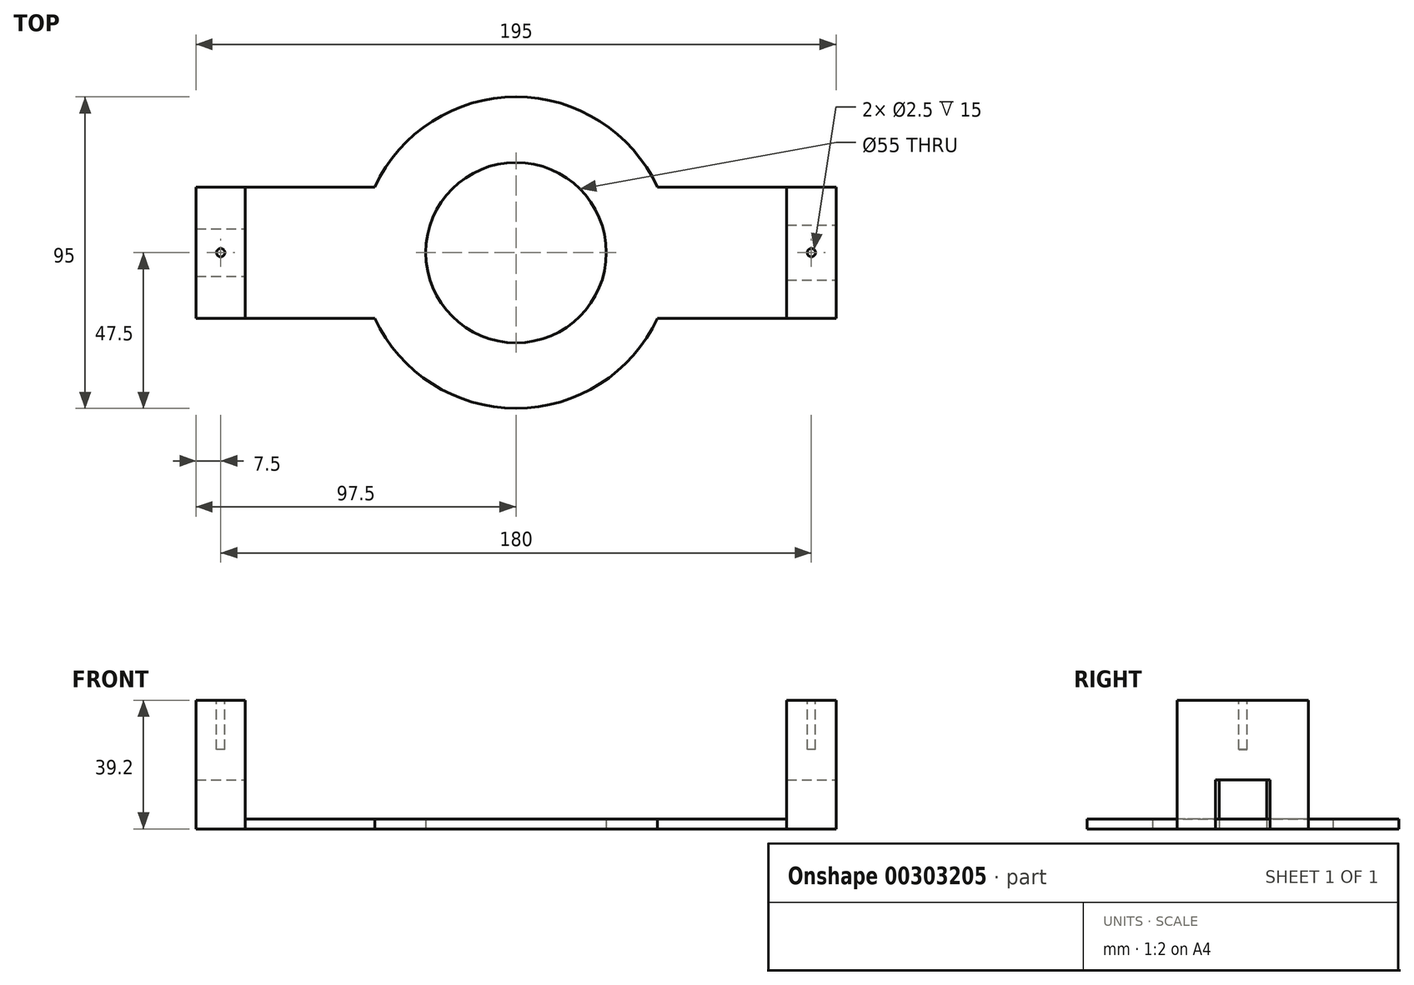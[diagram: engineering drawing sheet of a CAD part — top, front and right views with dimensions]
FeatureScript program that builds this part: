
annotation { "Feature Type Name" : "Feature", "Feature Type Description" : "" }
export const myFeature = defineFeature(function(context is Context, id is Id, definition is map)
    precondition{}
    {
        {
            var Q0;
            Q0=qCreatedBy(makeId("Top.planeOp"),FACE);
            var sketch = newSketch(context, id + "F0", { "sketchPlane" : qUnion([Q0])});
            skCircle(sketch, "E0", {"center": v(0, 0) * mm, "radius": 27.5 * mm});
            skCircle(sketch, "E1", {"center": v(0, 0) * mm, "radius": 47.5 * mm});
            skLineSegment(sketch, "E2", {"start": v(0, 0) * mm, "end": v(-90, 0) * mm});
            skLineSegment(sketch, "E3", {"start": v(0, 0) * mm, "end": v(90, 0) * mm});
            skLineSegment(sketch, "E4.bottom", {"start": v(-97.5, 20) * mm, "end": v(-82.5, 20) * mm});
            skLineSegment(sketch, "E4.top", {"start": v(-97.5, -20) * mm, "end": v(-82.5, -20) * mm});
            skLineSegment(sketch, "E4.left", {"start": v(-97.5, 20) * mm, "end": v(-97.5, -20) * mm});
            skLineSegment(sketch, "E4.right", {"start": v(-82.5, 20) * mm, "end": v(-82.5, -20) * mm});
            skPoint(sketch, "E4.middle", {"position": v(-90, 0) * mm});
            skLineSegment(sketch, "E5.bottom", {"start": v(82.5, 20) * mm, "end": v(97.5, 20) * mm});
            skLineSegment(sketch, "E5.top", {"start": v(82.5, -20) * mm, "end": v(97.5, -20) * mm});
            skLineSegment(sketch, "E5.left", {"start": v(82.5, 20) * mm, "end": v(82.5, -20) * mm});
            skLineSegment(sketch, "E5.right", {"start": v(97.5, 20) * mm, "end": v(97.5, -20) * mm});
            skPoint(sketch, "E5.middle", {"position": v(90, 0) * mm});
            skLineSegment(sketch, "E6.left", {"start": v(-82.5, 20) * mm, "end": v(-82.5, -20.66) * mm});
            skLineSegment(sketch, "E7.left", {"start": v(82.5, 20) * mm, "end": v(82.5, -20.66) * mm});
            skLineSegment(sketch, "E8", {"start": v(97.5, -20) * mm, "end": v(43.08, -20) * mm});
            skLineSegment(sketch, "E9", {"start": v(97.5, 20) * mm, "end": v(43.08, 20) * mm});
            skLineSegment(sketch, "E10", {"start": v(-97.5, -20) * mm, "end": v(-43.08, -20) * mm});
            skLineSegment(sketch, "E11", {"start": v(-97.5, 20) * mm, "end": v(-43.08, 20) * mm});
            skSolve(sketch);
        }
        {
            var Q0;
            {var subQ3=sQuery(id+"F0.wireOp",EDGE,"E4.bottom");Q0=makeQuery(id+"F0.imprint","IMPRINT",FACE,{"disambiguationData":[TD([[makeQuery(id+"F0.imprint","IMPRINT",EDGE,{"derivedFrom":subQ3}),-1.0]])]});}
            var Q1;
            {var subQ3=sQuery(id+"F0.wireOp",EDGE,"E5.bottom");Q1=makeQuery(id+"F0.imprint","IMPRINT",FACE,{"disambiguationData":[TD([[makeQuery(id+"F0.imprint","IMPRINT",EDGE,{"derivedFrom":subQ3}),-1.0]])]});}
            extrude(context, id + "F1", {"entities" : qUnion([Q0, Q1]), "depth" : 39.2 * mm, "offsetDistance" : 25 * mm});
        }
        {
            var Q0;
            {var subQ3=sQuery(id+"F0.wireOp",EDGE,"E9");Q0=makeQuery(id+"F0.imprint","IMPRINT",FACE,{"disambiguationData":[TD([[makeQuery(id+"F0.imprint","IMPRINT",EDGE,{"derivedFrom":subQ3}),1.0]])]});}
            var Q1;
            {var subQ3=sQuery(id+"F0.wireOp",EDGE,"E8");Q1=makeQuery(id+"F0.imprint","IMPRINT",FACE,{"disambiguationData":[TD([[makeQuery(id+"F0.imprint","IMPRINT",EDGE,{"derivedFrom":subQ3}),-1.0]])]});}
            var Q2;
            {var subQ4=sQuery(id+"F0.wireOp",EDGE,"E2");var subQ7=sQuery(id+"F0.wireOp",EDGE,"E0");var subQ8=makeQuery(id+"F0.imprint","INTERSECT",VERTEX,{"derivedFrom":[subQ7,subQ4]});Q2=makeQuery(id+"F0.imprint","IMPRINT",FACE,{"disambiguationData":[TD([[makeQuery(id+"F0.imprint","IMPRINT",EDGE,{"disambiguationData":[TD([[subQ8,-1.0]])],"derivedFrom":subQ7}),-1.0]])]});}
            var Q3;
            {var subQ0=sQuery(id+"F0.wireOp",EDGE,"E2");var subQ7=sQuery(id+"F0.wireOp",EDGE,"E0");var subQ9=makeQuery(id+"F0.imprint","INTERSECT",VERTEX,{"derivedFrom":[subQ7,subQ0]});Q3=makeQuery(id+"F0.imprint","IMPRINT",FACE,{"disambiguationData":[TD([[makeQuery(id+"F0.imprint","IMPRINT",EDGE,{"disambiguationData":[TD([[subQ9,1.0]])],"derivedFrom":subQ7}),-1.0]])]});}
            var Q4;
            {var subQ3=sQuery(id+"F0.wireOp",EDGE,"E11");Q4=makeQuery(id+"F0.imprint","IMPRINT",FACE,{"disambiguationData":[TD([[makeQuery(id+"F0.imprint","IMPRINT",EDGE,{"derivedFrom":subQ3}),-1.0]])]});}
            var Q5;
            {var subQ3=sQuery(id+"F0.wireOp",EDGE,"E10");Q5=makeQuery(id+"F0.imprint","IMPRINT",FACE,{"disambiguationData":[TD([[makeQuery(id+"F0.imprint","IMPRINT",EDGE,{"derivedFrom":subQ3}),1.0]])]});}
            extrude(context, id + "F2", {"entities" : qUnion([Q0, Q1, Q2, Q3, Q4, Q5]), "depth" : 3 * mm, "offsetDistance" : 25 * mm});
        }
        {
            var Q0;
            Q0=makeQuery(id+"F1.opExtrude","CAP_FACE",FACE,{"disambiguationData":[OSD([sQuery(id+"F0.wireOp",EDGE,"E4.bottom"),sQuery(id+"F0.wireOp",EDGE,"E4.top"),sQuery(id+"F0.wireOp",EDGE,"E4.left"),sQuery(id+"F0.wireOp",EDGE,"E4.right")])],"isStart":true});
            var sketch = newSketch(context, id + "F3", { "sketchPlane" : qUnion([Q0])});
            skLineSegment(sketch, "E12.bottom", {"start": v(-82.5, 0) * mm, "end": v(-97.5, 0) * mm});
            skLineSegment(sketch, "E12.top", {"start": v(-82.5, 0) * mm, "end": v(-97.5, 0) * mm});
            skLineSegment(sketch, "E12.left", {"start": v(-82.5, 0) * mm, "end": v(-82.5, 0) * mm});
            skLineSegment(sketch, "E12.right", {"start": v(-97.5, 0) * mm, "end": v(-97.5, 0) * mm});
            skLineSegment(sketch, "E13.bottom", {"start": v(-97.5, 7.23) * mm, "end": v(-82.5, 7.23) * mm});
            skLineSegment(sketch, "E13.top", {"start": v(-97.5, -7.23) * mm, "end": v(-82.5, -7.23) * mm});
            skLineSegment(sketch, "E13.left", {"start": v(-97.5, 7.23) * mm, "end": v(-97.5, -7.23) * mm});
            skLineSegment(sketch, "E13.right", {"start": v(-82.5, 7.23) * mm, "end": v(-82.5, -7.23) * mm});
            skPoint(sketch, "E13.middle", {"position": v(-90, 0) * mm});
            skSolve(sketch);
        }
        {
            var Q0;
            Q0 = qSketchRegion(id + "F3", true);
            extrude(context, id + "F4", {"entities" : qUnion([Q0]), "operationType" : NewBodyOperationType.REMOVE, "oppositeDirection" : true, "depth" : 15 * mm, "offsetDistance" : 25 * mm});
        }
        {
            var Q0;
            Q0=makeQuery(id+"F1.opExtrude","CAP_FACE",FACE,{"disambiguationData":[OSD([sQuery(id+"F0.wireOp",EDGE,"E5.bottom"),sQuery(id+"F0.wireOp",EDGE,"E5.top"),sQuery(id+"F0.wireOp",EDGE,"E5.left"),sQuery(id+"F0.wireOp",EDGE,"E5.right")])],"isStart":true});
            var sketch = newSketch(context, id + "F5", { "sketchPlane" : qUnion([Q0])});
            skLineSegment(sketch, "E14.bottom", {"start": v(82.5, 0) * mm, "end": v(97.5, 0) * mm});
            skLineSegment(sketch, "E14.top", {"start": v(82.5, 0) * mm, "end": v(97.5, 0) * mm});
            skLineSegment(sketch, "E14.left", {"start": v(82.5, 0) * mm, "end": v(82.5, 0) * mm});
            skLineSegment(sketch, "E14.right", {"start": v(97.5, 0) * mm, "end": v(97.5, 0) * mm});
            skLineSegment(sketch, "E15.bottom", {"start": v(82.5, 8.34) * mm, "end": v(97.5, 8.34) * mm});
            skLineSegment(sketch, "E15.top", {"start": v(82.5, -8.34) * mm, "end": v(97.5, -8.34) * mm});
            skLineSegment(sketch, "E15.left", {"start": v(82.5, 8.34) * mm, "end": v(82.5, -8.34) * mm});
            skLineSegment(sketch, "E15.right", {"start": v(97.5, 8.34) * mm, "end": v(97.5, -8.34) * mm});
            skPoint(sketch, "E15.middle", {"position": v(90, 0) * mm});
            skSolve(sketch);
        }
        {
            var Q0;
            Q0 = qSketchRegion(id + "F5", true);
            extrude(context, id + "F6", {"entities" : qUnion([Q0]), "operationType" : NewBodyOperationType.REMOVE, "oppositeDirection" : true, "depth" : 15 * mm, "offsetDistance" : 25 * mm});
        }
        {
            var Q0;
            Q0=makeQuery(id+"F1.opExtrude","CAP_FACE",FACE,{"disambiguationData":[OSD([sQuery(id+"F0.wireOp",EDGE,"E4.bottom"),sQuery(id+"F0.wireOp",EDGE,"E4.top"),sQuery(id+"F0.wireOp",EDGE,"E4.left"),sQuery(id+"F0.wireOp",EDGE,"E4.right")])],"isStart":false});
            var sketch = newSketch(context, id + "F7", { "sketchPlane" : qUnion([Q0])});
            skLineSegment(sketch, "E16", {"start": v(-97.5, 0) * mm, "end": v(-82.5, 0) * mm, "construction": true});
            skCircle(sketch, "E17", {"center": v(-90, 0) * mm, "radius": 1.25 * mm});
            skSolve(sketch);
        }
        {
            var Q0;
            Q0=makeQuery(id+"F7.imprint","IMPRINT",FACE,{"disambiguationData":[TD([[makeQuery(id+"F7.imprint","IMPRINT",EDGE,{"derivedFrom":sQuery(id+"F7.wireOp",EDGE,"E17")}),1.0]])]});
            extrude(context, id + "F8", {"entities" : qUnion([Q0]), "operationType" : NewBodyOperationType.REMOVE, "oppositeDirection" : true, "depth" : 15 * mm, "offsetDistance" : 25 * mm});
        }
        {
            var Q0;
            Q0=makeQuery(id+"F1.opExtrude","CAP_FACE",FACE,{"disambiguationData":[OSD([sQuery(id+"F0.wireOp",EDGE,"E5.bottom"),sQuery(id+"F0.wireOp",EDGE,"E5.top"),sQuery(id+"F0.wireOp",EDGE,"E5.left"),sQuery(id+"F0.wireOp",EDGE,"E5.right")])],"isStart":false});
            var sketch = newSketch(context, id + "F9", { "sketchPlane" : qUnion([Q0])});
            skLineSegment(sketch, "E18", {"start": v(82.5, 0) * mm, "end": v(97.5, 0) * mm, "construction": true});
            skCircle(sketch, "E19", {"center": v(90, 0) * mm, "radius": 1.25 * mm});
            skSolve(sketch);
        }
        {
            var Q0;
            Q0=makeQuery(id+"F9.imprint","IMPRINT",FACE,{"disambiguationData":[TD([[makeQuery(id+"F9.imprint","IMPRINT",EDGE,{"derivedFrom":sQuery(id+"F9.wireOp",EDGE,"E19")}),1.0]])]});
            extrude(context, id + "F10", {"entities" : qUnion([Q0]), "operationType" : NewBodyOperationType.REMOVE, "oppositeDirection" : true, "depth" : 15 * mm, "offsetDistance" : 25 * mm});
        }
    });
